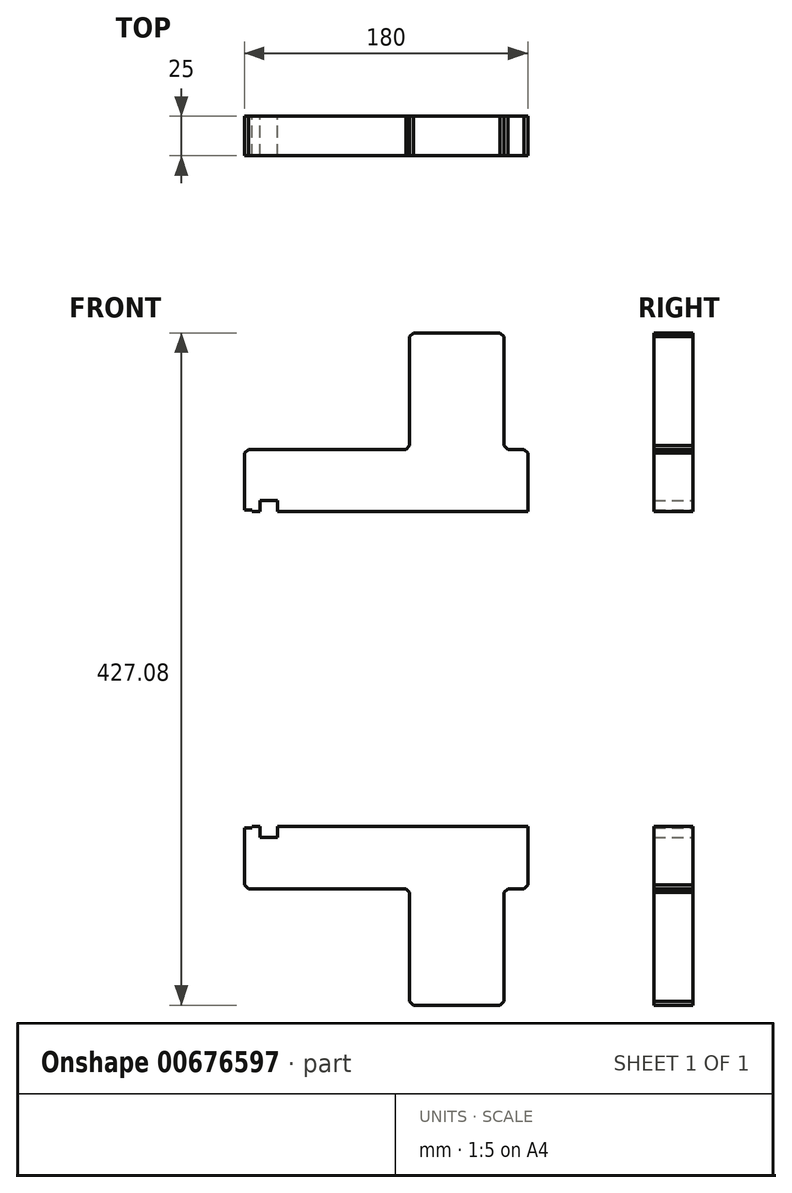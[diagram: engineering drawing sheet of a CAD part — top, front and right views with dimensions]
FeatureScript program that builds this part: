
annotation { "Feature Type Name" : "Feature", "Feature Type Description" : "" }
export const myFeature = defineFeature(function(context is Context, id is Id, definition is map)
    precondition{}
    {
        {
            var Q0;
            Q0=qCreatedBy(makeId("Front.planeOp"),FACE);
            var sketch = newSketch(context, id + "F0", { "sketchPlane" : qUnion([Q0])});
            skLineSegment(sketch, "E0", {"start": v(12.85, 100.04) * mm, "end": v(12.85, 107.04) * mm});
            skLineSegment(sketch, "E1", {"start": v(12.85, 107.04) * mm, "end": v(24, 107.04) * mm});
            skLineSegment(sketch, "E2", {"start": v(24, 107.04) * mm, "end": v(24, 100.04) * mm});
            skLineSegment(sketch, "E3", {"start": v(24, 100.04) * mm, "end": v(182.85, 100.04) * mm});
            skLineSegment(sketch, "E4", {"start": v(182.85, 100.04) * mm, "end": v(182.85, 139.54) * mm});
            skLineSegment(sketch, "E5", {"start": v(182.85, 139.54) * mm, "end": v(167.85, 139.54) * mm});
            skLineSegment(sketch, "E6", {"start": v(167.85, 139.54) * mm, "end": v(167.85, 213.54) * mm});
            skLineSegment(sketch, "E7", {"start": v(167.85, 213.54) * mm, "end": v(107.85, 213.54) * mm});
            skLineSegment(sketch, "E8", {"start": v(107.85, 213.54) * mm, "end": v(107.85, 139.54) * mm});
            skLineSegment(sketch, "E9", {"start": v(12.85, 100.04) * mm, "end": v(7.85, 100.04) * mm});
            skLineSegment(sketch, "E10", {"start": v(7.85, 100.04) * mm, "end": v(7.85, 100.9) * mm});
            skLineSegment(sketch, "E11", {"start": v(7.85, 100.9) * mm, "end": v(2.85, 100.9) * mm});
            skLineSegment(sketch, "E12", {"start": v(2.85, 100.9) * mm, "end": v(2.85, 139.54) * mm});
            skLineSegment(sketch, "E13", {"start": v(2.85, 139.54) * mm, "end": v(107.85, 139.54) * mm});
            skLineSegment(sketch, "E14", {"start": v(0, 0) * mm, "end": v(192.78, 0) * mm, "construction": true});
            skLineSegment(sketch, "E15.MirrorCS", {"start": v(24, -100.04) * mm, "end": v(182.85, -100.04) * mm});
            skLineSegment(sketch, "E16.MirrorCS", {"start": v(24, -107.04) * mm, "end": v(24, -100.04) * mm});
            skLineSegment(sketch, "E17.MirrorCS", {"start": v(12.85, -107.04) * mm, "end": v(24, -107.04) * mm});
            skLineSegment(sketch, "E18.MirrorCS", {"start": v(12.85, -100.04) * mm, "end": v(12.85, -107.04) * mm});
            skLineSegment(sketch, "E19.MirrorCS", {"start": v(12.85, -100.04) * mm, "end": v(7.85, -100.04) * mm});
            skLineSegment(sketch, "E20.MirrorCS", {"start": v(7.85, -100.04) * mm, "end": v(7.85, -100.9) * mm});
            skLineSegment(sketch, "E21.MirrorCS", {"start": v(7.85, -100.9) * mm, "end": v(2.85, -100.9) * mm});
            skLineSegment(sketch, "E22.MirrorCS", {"start": v(2.85, -100.9) * mm, "end": v(2.85, -139.54) * mm});
            skLineSegment(sketch, "E23.MirrorCS", {"start": v(2.85, -139.54) * mm, "end": v(107.85, -139.54) * mm});
            skLineSegment(sketch, "E24.MirrorCS", {"start": v(107.85, -213.54) * mm, "end": v(107.85, -139.54) * mm});
            skLineSegment(sketch, "E25.MirrorCS", {"start": v(167.85, -213.54) * mm, "end": v(107.85, -213.54) * mm});
            skLineSegment(sketch, "E26.MirrorCS", {"start": v(167.85, -139.54) * mm, "end": v(167.85, -213.54) * mm});
            skLineSegment(sketch, "E27.MirrorCS", {"start": v(182.85, -139.54) * mm, "end": v(167.85, -139.54) * mm});
            skLineSegment(sketch, "E28.MirrorCS", {"start": v(182.85, -100.04) * mm, "end": v(182.85, -139.54) * mm});
            skLineSegment(sketch, "E29.bottom", {"start": v(-42.5, 99.95) * mm, "end": v(307.5, 99.95) * mm});
            skLineSegment(sketch, "E29.top", {"start": v(-42.5, -99.95) * mm, "end": v(307.5, -99.95) * mm});
            skLineSegment(sketch, "E29.left", {"start": v(-42.5, 99.95) * mm, "end": v(-42.5, -99.95) * mm});
            skLineSegment(sketch, "E29.right", {"start": v(307.5, 99.95) * mm, "end": v(307.5, -99.95) * mm});
            skSolve(sketch);
        }
        {
            var Q0;
            Q0=makeQuery(id+"F0.imprint","IMPRINT",FACE,{"disambiguationData":[TD([[makeQuery(id+"F0.imprint","IMPRINT",EDGE,{"derivedFrom":sQuery(id+"F0.wireOp",EDGE,"E0")}),1.0]])]});
            var Q1;
            Q1=makeQuery(id+"F0.imprint","IMPRINT",FACE,{"disambiguationData":[TD([[makeQuery(id+"F0.imprint","IMPRINT",EDGE,{"derivedFrom":sQuery(id+"F0.wireOp",EDGE,"E15.MirrorCS")}),-1.0]])]});
            extrude(context, id + "F1", {"entities" : qUnion([Q0, Q1]), "depth" : 25 * mm, "offsetDistance" : 25 * mm});
        }
        {
            var Q0;
            Q0=makeQuery(id+"F1.opExtrude","SWEPT_EDGE",EDGE,{"disambiguationData":[OSD([sQuery(id+"F0.wireOp",EDGE,"E12"),sQuery(id+"F0.wireOp",EDGE,"E13")])]});
            var Q1;
            Q1=makeQuery(id+"F1.opExtrude","SWEPT_EDGE",EDGE,{"disambiguationData":[OSD([sQuery(id+"F0.wireOp",EDGE,"E8"),sQuery(id+"F0.wireOp",EDGE,"E13")])]});
            var Q2;
            Q2=makeQuery(id+"F1.opExtrude","SWEPT_EDGE",EDGE,{"disambiguationData":[OSD([sQuery(id+"F0.wireOp",EDGE,"E7"),sQuery(id+"F0.wireOp",EDGE,"E8")])]});
            var Q3;
            Q3=makeQuery(id+"F1.opExtrude","SWEPT_EDGE",EDGE,{"disambiguationData":[OSD([sQuery(id+"F0.wireOp",EDGE,"E6"),sQuery(id+"F0.wireOp",EDGE,"E7")])]});
            var Q4;
            Q4=makeQuery(id+"F1.opExtrude","SWEPT_EDGE",EDGE,{"disambiguationData":[OSD([sQuery(id+"F0.wireOp",EDGE,"E5"),sQuery(id+"F0.wireOp",EDGE,"E6")])]});
            var Q5;
            Q5=makeQuery(id+"F1.opExtrude","SWEPT_EDGE",EDGE,{"disambiguationData":[OSD([sQuery(id+"F0.wireOp",EDGE,"E4"),sQuery(id+"F0.wireOp",EDGE,"E5")])]});
            var Q6;
            Q6=makeQuery(id+"F1.opExtrude","SWEPT_EDGE",EDGE,{"disambiguationData":[OSD([sQuery(id+"F0.wireOp",EDGE,"E22.MirrorCS"),sQuery(id+"F0.wireOp",EDGE,"E23.MirrorCS")])]});
            var Q7;
            Q7=makeQuery(id+"F1.opExtrude","SWEPT_EDGE",EDGE,{"disambiguationData":[OSD([sQuery(id+"F0.wireOp",EDGE,"E23.MirrorCS"),sQuery(id+"F0.wireOp",EDGE,"E24.MirrorCS")])]});
            var Q8;
            Q8=makeQuery(id+"F1.opExtrude","SWEPT_EDGE",EDGE,{"disambiguationData":[OSD([sQuery(id+"F0.wireOp",EDGE,"E24.MirrorCS"),sQuery(id+"F0.wireOp",EDGE,"E25.MirrorCS")])]});
            var Q9;
            Q9=makeQuery(id+"F1.opExtrude","SWEPT_EDGE",EDGE,{"disambiguationData":[OSD([sQuery(id+"F0.wireOp",EDGE,"E25.MirrorCS"),sQuery(id+"F0.wireOp",EDGE,"E26.MirrorCS")])]});
            var Q10;
            Q10=makeQuery(id+"F1.opExtrude","SWEPT_EDGE",EDGE,{"disambiguationData":[OSD([sQuery(id+"F0.wireOp",EDGE,"E26.MirrorCS"),sQuery(id+"F0.wireOp",EDGE,"E27.MirrorCS")])]});
            var Q11;
            Q11=makeQuery(id+"F1.opExtrude","SWEPT_EDGE",EDGE,{"disambiguationData":[OSD([sQuery(id+"F0.wireOp",EDGE,"E27.MirrorCS"),sQuery(id+"F0.wireOp",EDGE,"E28.MirrorCS")])]});
            chamfer(context, id + "F2", {"entities" : qUnion([Q0, Q1, Q2, Q3, Q4, Q5, Q6, Q7, Q8, Q9, Q10, Q11]), "width" : 2.5 * mm, "tangentPropagation" : true});
        }
    });
